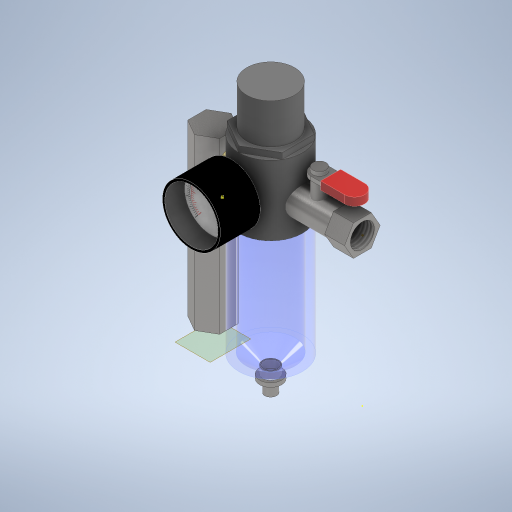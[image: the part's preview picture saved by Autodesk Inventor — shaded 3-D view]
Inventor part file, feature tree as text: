
AUTODESK INVENTOR PART (.ipt)
format: ipt  version: 2024 (Build 280153000, 153)  size: 630,784 bytes
history: native  units: mm
features: extrude x22, sketch x20, plane x5, split x2, thread x2, other x2, revolve x1, projected_geometry x1
ambient origin geometry x8: Origin, YZ Plane, XZ Plane, XY Plane, X Axis, Y Axis, Z Axis, Center Point
bodies: Solid1 (feature_tree), Solid6 (feature_tree), Solid7 (feature_tree), Solid8 (feature_tree), Solid9 (feature_tree), Solid10 (feature_tree), Solid2 (feature_tree), Solid3 (feature_tree), Solid4 (feature_tree), Solid5 (feature_tree)
feature tree (55):
  extrude  "Extrusion1"  Depth=85.0mm TaperAngle=0.0deg
  extrude  "Extrusion2"  Depth=3.0mm TaperAngle=0.0deg
  extrude  "Extrusion3"  Depth=10.0mm TaperAngle=0.0deg
  extrude  "Extrusion4"  Depth=3.0mm TaperAngle=0.0deg
  split  "Split1"
  split  "Split2"
  extrude  "Extrusion5"  Depth=20.0mm TaperAngle=0.0deg
  extrude  "Extrusion6"  Depth=10.0mm
  extrude  "Extrusion7"  Depth=10.0mm
  plane  "Work Plane1"
  extrude  "Extrusion8"  Depth=10.0mm TaperAngle=0.0deg
  plane  "Work Plane2"
  extrude  "Extrusion9"  Depth=4.5mm
  extrude  "Extrusion10"  TaperAngle=90.0deg  [1 undecoded]
  thread  "Thread1"  [1 undecoded]
  plane  "Work Plane3"
  extrude  "Extrusion11"  Depth=20.0mm TaperAngle=0.0deg
  revolve  "Revolution1"  [1 undecoded]
  extrude  "Extrusion12"  TaperAngle=0.0deg  [1 undecoded]
  plane  "Work Plane4"
  extrude  "Extrusion13"  Depth=7.0mm
  extrude  "Extrusion14"  Depth=4.0mm
  extrude  "Extrusion15"  Depth=6.0mm
  other  "Decal1"
  extrude  "Extrusion16"  Depth=10.949369mm
  extrude  "Extrusion17"  Depth=14.0mm
  plane  "Work Plane5"
  extrude  "Extrusion18"  Depth=8.0mm TaperAngle=0.0deg
  extrude  "Extrusion19"  Depth=3.0mm
  extrude  "Extrusion20"  Depth=5.0mm
  extrude  "Extrusion21"  TaperAngle=90.0deg  [1 undecoded]
  thread  "Thread2"  [1 undecoded]
  extrude  "Extrusion22"  TaperAngle=90.0deg  [1 undecoded]
  sketch  "Sketch30"  dims[d82=29.041478mm d83=26.679106mm d84=5.0mm d85=90.0deg d86=5.0mm d87=90.0deg d88=1.0mm d89=3.0mm d90=0.0mm d91=0.0mm]
  sketch  "Sketch1"  dims[d0=8.0mm d1=85.0mm d2=0.0mm]
  sketch  "Sketch3"  dims[d3=5.0mm d4=3.0mm d5=0.0mm]
  sketch  "Sketch4"  dims[d6=5.0mm d7=0.0mm d8=10.0mm d9=25.0mm d10=0.0mm d11=0.0mm]
  sketch  "Sketch6"  dims[d12=10.0mm d13=0.0mm d14=3.0mm d15=0.0mm]
  sketch  "Sketch7"  dims[d16=20.0mm d17=0.0mm d18=30.0mm d19=0.0mm]
  sketch  "Sketch9"  dims[d20=10.0mm d21=0.0mm d22=8.420912mm d23=14.0mm]
  sketch  "Sketch10"  dims[d24=12.25mm d25=10.0mm d26=0.0mm d27=0.0mm d28=12.0mm]
  sketch  "Sketch13"  dims[d29=10.0mm d30=0.0mm d31=10.0mm d32=0.0mm]
  sketch  "Sketch14"  dims[d33=-4.0mm d34=4.5mm]
  sketch  "Sketch15"  dims[d35=2.0mm d36=0.0mm d37=90.0deg d38=10.0mm d39=0.0mm]
  projected_geometry  "Projected Loop1"
  sketch  "Sketch16"  dims[d40=8.0mm d41=0.0mm d42=20.0mm d43=0.0mm]
  sketch  "Sketch17"  dims[d44=10.0mm d45=0.0mm d59=1.0mm d60=0.0mm]
  sketch  "Sketch19"  dims[d61=8.0mm d62=0.0mm d63=0.0mm]
  sketch  "Sketch20"  dims[d64=9.0mm d65=7.0mm]
  sketch  "Sketch21"  dims[d66=4.0mm d67=0.0mm d68=11.0mm]
  sketch  "Sketch22"  dims[d69=2.0mm d70=0.0mm d71=6.0mm]
  other  "Image1"
  sketch  "Sketch26"  dims[d72=6.0mm d73=0.0mm d74=10.949369mm]
  sketch  "Sketch27"  dims[d76=14.0mm d77=14.0mm]
  sketch  "Sketch29"  dims[d78=3.0mm d79=0.0mm d80=8.0mm d81=0.0mm]
note: 7 required parameter values undecoded (feature->parameter linkage not recoverable at this tier; creation-order binding heuristic only, values carry confidence <= 0.55)